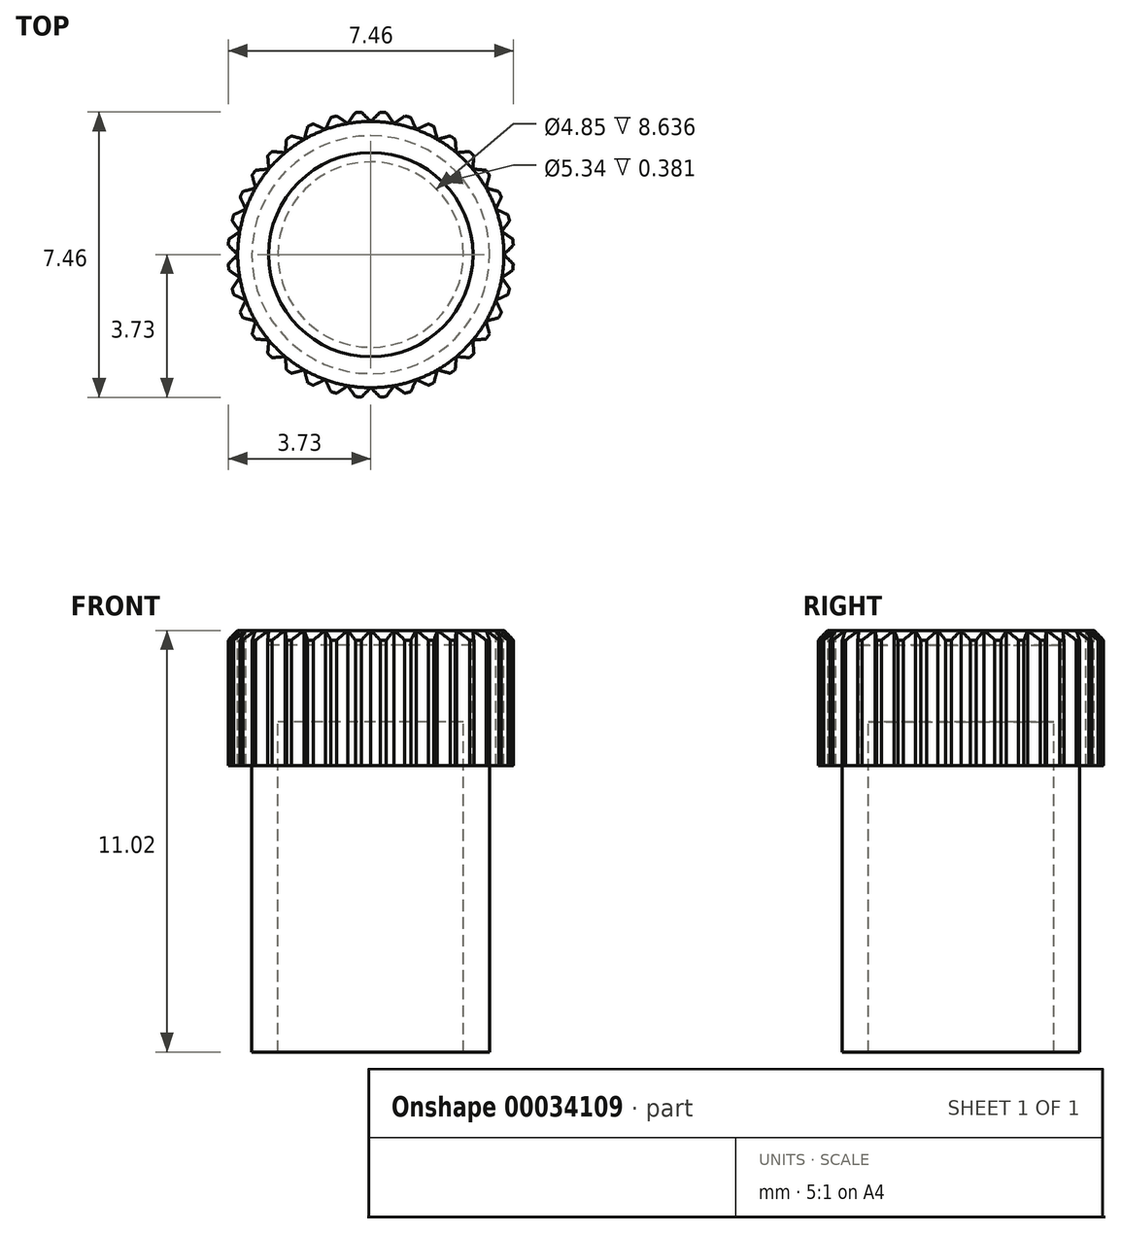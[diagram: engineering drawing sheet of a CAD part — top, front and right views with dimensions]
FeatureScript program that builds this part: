
annotation { "Feature Type Name" : "Feature", "Feature Type Description" : "" }
export const myFeature = defineFeature(function(context is Context, id is Id, definition is map)
    precondition{}
    {
        {
            var Q0;
            Q0=qCreatedBy(makeId("Front.planeOp"),FACE);
            var sketch = newSketch(context, id + "F0", { "sketchPlane" : qUnion([Q0])});
            skLineSegment(sketch, "E0", {"start": v(0, 10.64) * mm, "end": v(0, 8.64) * mm});
            skLineSegment(sketch, "E1", {"start": v(0, 8.64) * mm, "end": v(2.43, 8.64) * mm});
            skLineSegment(sketch, "E2", {"start": v(2.43, 8.64) * mm, "end": v(2.43, 0) * mm});
            skLineSegment(sketch, "E3", {"start": v(2.43, 0) * mm, "end": v(3.11, 0) * mm});
            skLineSegment(sketch, "E4", {"start": v(3.11, 0) * mm, "end": v(3.11, 7.5) * mm});
            skLineSegment(sketch, "E5", {"start": v(3.11, 7.5) * mm, "end": v(3.73, 7.5) * mm});
            skLineSegment(sketch, "E6", {"start": v(3.73, 7.5) * mm, "end": v(3.73, 11.02) * mm});
            skLineSegment(sketch, "E7", {"start": v(3.73, 11.02) * mm, "end": v(2.67, 11.02) * mm});
            skLineSegment(sketch, "E8", {"start": v(2.67, 11.02) * mm, "end": v(2.67, 10.64) * mm});
            skLineSegment(sketch, "E9", {"start": v(2.67, 10.64) * mm, "end": v(0, 10.64) * mm});
            skSolve(sketch);
        }
        {
            var Q0;
            Q0 = qSketchRegion(id + "F0", true);
            var Q1;
            Q1=sQuery(id+"F0.wireOp",EDGE,"E0");
            revolve(context, id + "F1", {"entities" : qUnion([Q0]), "axis" : qUnion([Q1]), "revolveType" : RevolveType.FULL});
        }
        {
            var Q0;
            Q0=makeQuery(id+"F1.opRevolve","SWEPT_EDGE",EDGE,{"disambiguationData":[OSD([sQuery(id+"F0.wireOp",EDGE,"E6"),sQuery(id+"F0.wireOp",EDGE,"E7")])]});
            chamfer(context, id + "F2", {"entities" : qUnion([Q0]), "width" : 0.25 * mm, "tangentPropagation" : true});
        }
        {
            var Q0;
            Q0=makeQuery(id+"F1.opRevolve","SWEPT_FACE",FACE,{"disambiguationData":[OSD([sQuery(id+"F0.wireOp",EDGE,"E7")])]});
            var sketch = newSketch(context, id + "F3", { "sketchPlane" : qUnion([Q0])});
            skLineSegment(sketch, "E10", {"start": v(0, 3.48) * mm, "end": v(-0.41, 3.9) * mm});
            skLineSegment(sketch, "E11", {"start": v(-0.41, 3.9) * mm, "end": v(0.41, 3.9) * mm});
            skLineSegment(sketch, "E12", {"start": v(0.41, 3.9) * mm, "end": v(0, 3.48) * mm});
            skSolve(sketch);
        }
        {
            var Q0;
            Q0 = qSketchRegion(id + "F3", true);
            var Q1;
            Q1=makeQuery(id+"F1.opRevolve","SWEPT_FACE",FACE,{"disambiguationData":[OSD([sQuery(id+"F0.wireOp",EDGE,"E5")])]});
            extrude(context, id + "F4", {"entities" : qUnion([Q0]), "endBound" : BoundingType.UP_TO_SURFACE, "oppositeDirection" : true, "endBoundEntityFace" : qUnion([Q1]), "depth" : 25.4 * mm});
        }
        {
            var Q0;
            Q0=makeQuery(id+"F4.opExtrude","SWEPT_BODY",BODY,{"disambiguationData":[OSD([sQuery(id+"F3.wireOp",EDGE,"E10"),sQuery(id+"F3.wireOp",EDGE,"E11"),sQuery(id+"F3.wireOp",EDGE,"E12")])]});
            var Q1;
            Q1=makeQuery(id+"F4.boolean.opBoolean","COPY",FACE,{"derivedFrom":makeQuery(id+"F4.opExtrude","SWEPT_FACE",FACE,{"disambiguationData":[OSD([sQuery(id+"F3.wireOp",EDGE,"E10")])]})});
            var Q2;
            Q2=makeQuery(id+"F1.opRevolve","SWEPT_FACE",FACE,{"disambiguationData":[OSD([sQuery(id+"F0.wireOp",EDGE,"E4")])]});
            circularPattern(context, id + "F5", {"operationType" : NewBodyOperationType.REMOVE, "entities" : qUnion([Q0]), "axis" : qUnion([Q2]), "angle" : 10 * degree, "instanceCount" : 36});
        }
    });
